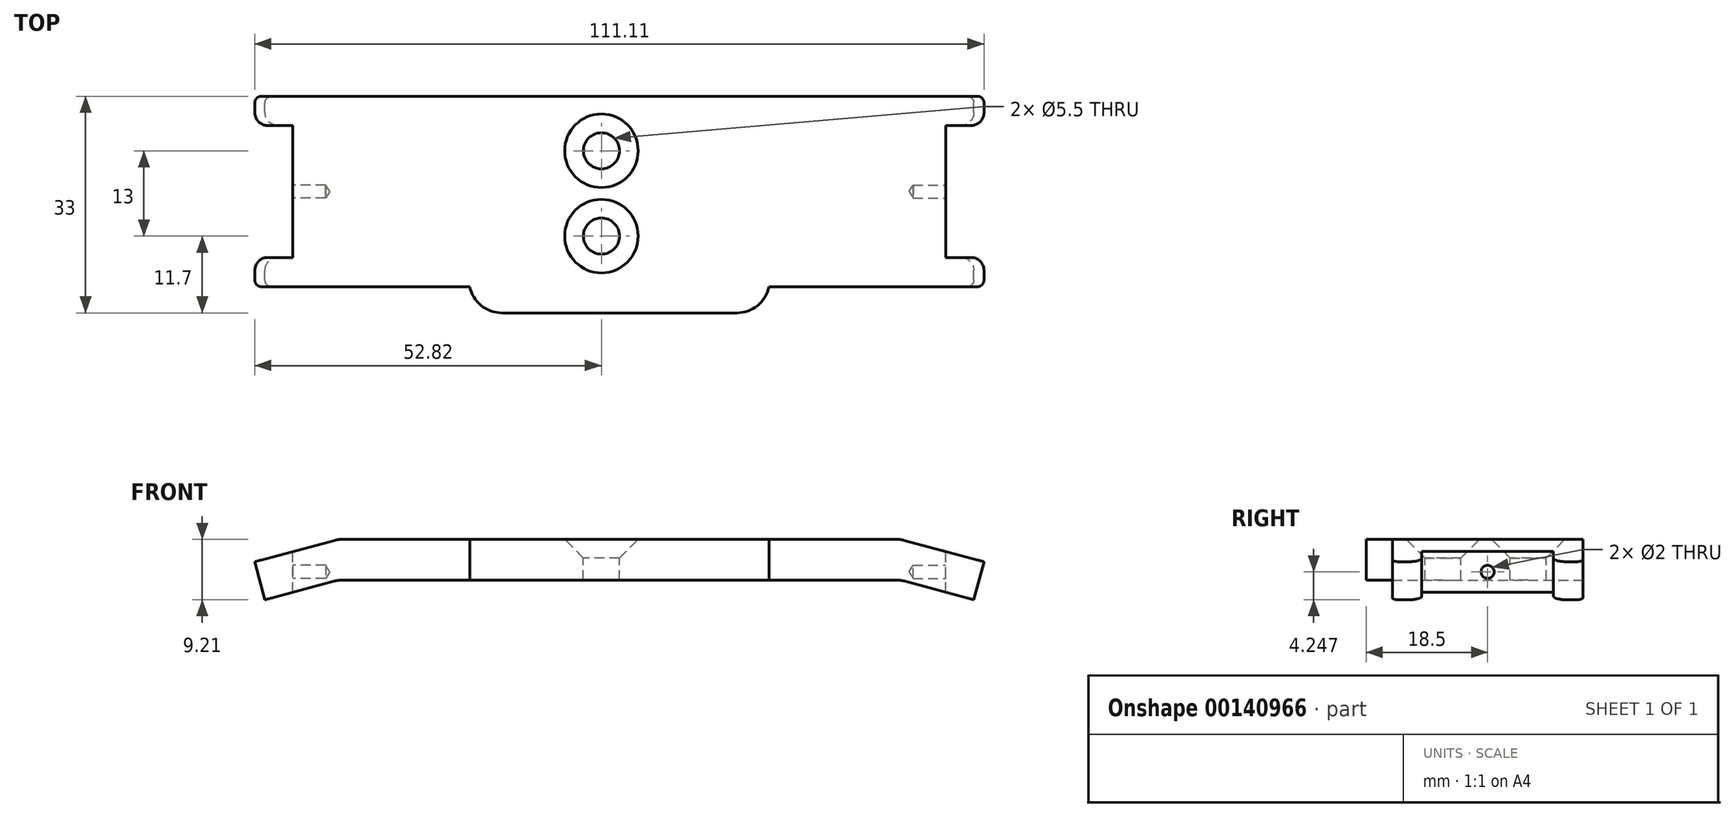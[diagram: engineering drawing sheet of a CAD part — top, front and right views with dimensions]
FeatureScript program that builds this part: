
annotation { "Feature Type Name" : "Feature", "Feature Type Description" : "" }
export const myFeature = defineFeature(function(context is Context, id is Id, definition is map)
    precondition{}
    {
        {
            var Q0;
            Q0=qCreatedBy(makeId("Front.planeOp"),FACE);
            var sketch = newSketch(context, id + "F0", { "sketchPlane" : qUnion([Q0])});
            skLineSegment(sketch, "E0", {"start": v(-40.07, 20.76) * mm, "end": v(45.54, 20.76) * mm});
            skLineSegment(sketch, "E1", {"start": v(45.54, 20.76) * mm, "end": v(58.3, 17.34) * mm});
            skLineSegment(sketch, "E2", {"start": v(58.3, 17.34) * mm, "end": v(56.74, 11.55) * mm});
            skLineSegment(sketch, "E3", {"start": v(56.74, 11.55) * mm, "end": v(45.54, 14.55) * mm});
            skLineSegment(sketch, "E4", {"start": v(45.54, 14.55) * mm, "end": v(-40.07, 14.55) * mm});
            skLineSegment(sketch, "E5", {"start": v(-40.07, 14.55) * mm, "end": v(-51.26, 11.55) * mm});
            skLineSegment(sketch, "E6", {"start": v(-51.26, 11.55) * mm, "end": v(-52.82, 17.34) * mm});
            skLineSegment(sketch, "E7", {"start": v(-52.82, 17.34) * mm, "end": v(-40.07, 20.76) * mm});
            skSolve(sketch);
        }
        {
            var Q0;
            Q0=makeQuery(id+"F0.imprint","IMPRINT",FACE,{"disambiguationData":[TD([[makeQuery(id+"F0.imprint","IMPRINT",EDGE,{"derivedFrom":sQuery(id+"F0.wireOp",EDGE,"E0")}),-1.0]])]});
            extrude(context, id + "F1", {"entities" : qUnion([Q0]), "depth" : 29 * mm});
        }
        {
            var Q0;
            Q0=makeQuery(id+"F1.opExtrude","CAP_FACE",FACE,{"disambiguationData":[OSD([sQuery(id+"F0.wireOp",EDGE,"E0"),sQuery(id+"F0.wireOp",EDGE,"E1"),sQuery(id+"F0.wireOp",EDGE,"E2"),sQuery(id+"F0.wireOp",EDGE,"E3"),sQuery(id+"F0.wireOp",EDGE,"E4"),sQuery(id+"F0.wireOp",EDGE,"E5"),sQuery(id+"F0.wireOp",EDGE,"E6"),sQuery(id+"F0.wireOp",EDGE,"E7")])],"isStart":false});
            var sketch = newSketch(context, id + "F2", { "sketchPlane" : qUnion([Q0])});
            skLineSegment(sketch, "E8.bottom", {"start": v(-20.07, 20.76) * mm, "end": v(25.54, 20.76) * mm});
            skLineSegment(sketch, "E8.top", {"start": v(-20.07, 14.55) * mm, "end": v(25.54, 14.55) * mm});
            skLineSegment(sketch, "E8.left", {"start": v(-20.07, 20.76) * mm, "end": v(-20.07, 14.55) * mm});
            skLineSegment(sketch, "E8.right", {"start": v(25.54, 20.76) * mm, "end": v(25.54, 14.55) * mm});
            skSolve(sketch);
        }
        {
            var Q0;
            Q0=makeQuery(id+"F2.imprint","IMPRINT",FACE,{"disambiguationData":[TD([[makeQuery(id+"F2.imprint","IMPRINT",EDGE,{"derivedFrom":sQuery(id+"F2.wireOp",EDGE,"E8.bottom")}),-1.0]])]});
            extrude(context, id + "F3", {"entities" : qUnion([Q0]), "operationType" : NewBodyOperationType.ADD, "depth" : 4 * mm, "offsetDistance" : 25 * mm});
        }
        {
            var Q0;
            Q0=makeQuery(id+"F3.boolean.opBoolean","MERGE",FACE,{"derivedFrom":[makeQuery(id+"F1.opExtrude","SWEPT_FACE",FACE,{"disambiguationData":[OSD([sQuery(id+"F0.wireOp",EDGE,"E0")])]}),makeQuery(id+"F3.opExtrude","SWEPT_FACE",FACE,{"disambiguationData":[OSD([sQuery(id+"F2.wireOp",EDGE,"E8.bottom")])]})]});
            var sketch = newSketch(context, id + "F4", { "sketchPlane" : qUnion([Q0])});
            skLineSegment(sketch, "E9.bottom", {"start": v(-61.47, -4.45) * mm, "end": v(-47.02, -4.45) * mm});
            skLineSegment(sketch, "E9.top", {"start": v(-61.47, -24.55) * mm, "end": v(-47.02, -24.55) * mm});
            skLineSegment(sketch, "E9.left", {"start": v(-61.47, -4.45) * mm, "end": v(-61.47, -24.55) * mm});
            skLineSegment(sketch, "E9.right", {"start": v(-47.02, -4.45) * mm, "end": v(-47.02, -24.55) * mm});
            skLineSegment(sketch, "E10.bottom", {"start": v(52.5, -4.45) * mm, "end": v(64.3, -4.45) * mm});
            skLineSegment(sketch, "E10.top", {"start": v(52.5, -24.55) * mm, "end": v(64.3, -24.55) * mm});
            skLineSegment(sketch, "E10.left", {"start": v(64.3, -4.45) * mm, "end": v(64.3, -24.55) * mm});
            skLineSegment(sketch, "E10.right", {"start": v(52.5, -4.45) * mm, "end": v(52.5, -24.55) * mm});
            skSolve(sketch);
        }
        {
            var Q0;
            Q0=makeQuery(id+"F4.imprint","IMPRINT",FACE,{"disambiguationData":[TD([[makeQuery(id+"F4.imprint","IMPRINT",EDGE,{"derivedFrom":sQuery(id+"F4.wireOp",EDGE,"E9.bottom")}),-1.0]])]});
            var Q1;
            Q1=makeQuery(id+"F4.imprint","IMPRINT",FACE,{"disambiguationData":[TD([[makeQuery(id+"F4.imprint","IMPRINT",EDGE,{"derivedFrom":sQuery(id+"F4.wireOp",EDGE,"E10.bottom")}),-1.0]])]});
            extrude(context, id + "F5", {"entities" : qUnion([Q0, Q1]), "operationType" : NewBodyOperationType.REMOVE, "oppositeDirection" : true, "depth" : 25 * mm});
        }
        {
            var Q0;
            Q0=makeQuery(id+"F5.boolean.opBoolean","COPY",FACE,{"derivedFrom":makeQuery(id+"F5.opExtrude","SWEPT_FACE",FACE,{"disambiguationData":[OSD([sQuery(id+"F4.wireOp",EDGE,"E9.right")])]})});
            var sketch = newSketch(context, id + "F6", { "sketchPlane" : qUnion([Q0])});
            skCircle(sketch, "E11", {"center": v(14.5, 15.8) * mm, "radius": 1.07 * mm});
            skSolve(sketch);
        }
        {
            var Q0;
            Q0=sQuery(id+"F6.wireOp",VERTEX,"E11.center");
            var Q1;
            Q1=makeQuery(id+"F1.opExtrude","SWEPT_BODY",BODY,{"disambiguationData":[OSD([sQuery(id+"F0.wireOp",EDGE,"E0"),sQuery(id+"F0.wireOp",EDGE,"E1"),sQuery(id+"F0.wireOp",EDGE,"E2"),sQuery(id+"F0.wireOp",EDGE,"E3"),sQuery(id+"F0.wireOp",EDGE,"E4"),sQuery(id+"F0.wireOp",EDGE,"E5"),sQuery(id+"F0.wireOp",EDGE,"E6"),sQuery(id+"F0.wireOp",EDGE,"E7")])]});
            hole(context, id + "F7", {"style" : HoleStyle.SIMPLE, "endStyle" : HoleEndStyle.BLIND, "holeDiameter" : 2 * mm, "holeDepth" : 5 * mm, "isTappedThrough" : true, "tappedDepth" : 12 * mm, "tapClearance" : 3, "locations" : qUnion([Q0]), "scope" : qUnion([Q1])});
        }
        {
            var Q0;
            Q0=makeQuery(id+"F1.opExtrude","SWEPT_EDGE",EDGE,{"disambiguationData":[OSD([sQuery(id+"F0.wireOp",EDGE,"E0"),sQuery(id+"F0.wireOp",EDGE,"E1")])]});
            var Q1;
            Q1=makeQuery(id+"F1.opExtrude","SWEPT_EDGE",EDGE,{"disambiguationData":[OSD([sQuery(id+"F0.wireOp",EDGE,"E0"),sQuery(id+"F0.wireOp",EDGE,"E7")])]});
            var Q2;
            Q2=makeQuery(id+"F3.opExtrude","CAP_EDGE",EDGE,{"disambiguationData":[OSD([sQuery(id+"F2.wireOp",EDGE,"E8.left")])],"isStart":false});
            var Q3;
            Q3=makeQuery(id+"F3.opExtrude","CAP_EDGE",EDGE,{"disambiguationData":[OSD([sQuery(id+"F2.wireOp",EDGE,"E8.right")])],"isStart":false});
            var Q4;
            Q4=makeQuery(id+"F1.opExtrude","SWEPT_EDGE",EDGE,{"disambiguationData":[OSD([sQuery(id+"F0.wireOp",EDGE,"E4"),sQuery(id+"F0.wireOp",EDGE,"E5")])]});
            var Q5;
            Q5=makeQuery(id+"F1.opExtrude","SWEPT_EDGE",EDGE,{"disambiguationData":[OSD([sQuery(id+"F0.wireOp",EDGE,"E3"),sQuery(id+"F0.wireOp",EDGE,"E4")])]});
            fillet(context, id + "F8", {"entities" : qUnion([Q0, Q1, Q2, Q3, Q4, Q5]), "radius" : 5 * mm, "tangentPropagation" : true, "allowEdgeOverflow" : false});
        }
        {
            var Q0;
            Q0=makeQuery(id+"F1.opExtrude","CAP_EDGE",EDGE,{"disambiguationData":[OSD([sQuery(id+"F0.wireOp",EDGE,"E6")])],"isStart":false});
            var Q1;
            Q1=makeQuery(id+"F1.opExtrude","CAP_EDGE",EDGE,{"disambiguationData":[OSD([sQuery(id+"F0.wireOp",EDGE,"E6")])],"isStart":true});
            var Q2;
            Q2=makeQuery(id+"F1.opExtrude","CAP_EDGE",EDGE,{"disambiguationData":[OSD([sQuery(id+"F0.wireOp",EDGE,"E2")])],"isStart":true});
            var Q3;
            Q3=makeQuery(id+"F1.opExtrude","CAP_EDGE",EDGE,{"disambiguationData":[OSD([sQuery(id+"F0.wireOp",EDGE,"E2")])],"isStart":false});
            fillet(context, id + "F9", {"entities" : qUnion([Q0, Q1, Q2, Q3]), "radius" : 1 * mm, "tangentPropagation" : true, "allowEdgeOverflow" : false});
        }
        {
            var Q0;
            Q0=makeQuery(id+"F5.boolean.opBoolean","COPY",FACE,{"derivedFrom":makeQuery(id+"F5.opExtrude","SWEPT_FACE",FACE,{"disambiguationData":[OSD([sQuery(id+"F4.wireOp",EDGE,"E10.right")])]})});
            var sketch = newSketch(context, id + "F10", { "sketchPlane" : qUnion([Q0])});
            skCircle(sketch, "E12", {"center": v(-14.5, 15.8) * mm, "radius": 1.68 * mm});
            skSolve(sketch);
        }
        {
            var Q0;
            Q0=sQuery(id+"F10.wireOp",VERTEX,"E12.center");
            var Q1;
            Q1=makeQuery(id+"F1.opExtrude","SWEPT_BODY",BODY,{"disambiguationData":[OSD([sQuery(id+"F0.wireOp",EDGE,"E0"),sQuery(id+"F0.wireOp",EDGE,"E1"),sQuery(id+"F0.wireOp",EDGE,"E2"),sQuery(id+"F0.wireOp",EDGE,"E3"),sQuery(id+"F0.wireOp",EDGE,"E4"),sQuery(id+"F0.wireOp",EDGE,"E5"),sQuery(id+"F0.wireOp",EDGE,"E6"),sQuery(id+"F0.wireOp",EDGE,"E7")])]});
            hole(context, id + "F11", {"style" : HoleStyle.SIMPLE, "endStyle" : HoleEndStyle.BLIND, "holeDiameter" : 2 * mm, "holeDepth" : 5 * mm, "isTappedThrough" : true, "tappedDepth" : 12 * mm, "tapClearance" : 3, "locations" : qUnion([Q0]), "scope" : qUnion([Q1])});
        }
        {
            var Q0;
            Q0=makeQuery(id+"F5.boolean.opBoolean","INTERSECT",EDGE,{"derivedFrom":[makeQuery(id+"F1.opExtrude","SWEPT_FACE",FACE,{"disambiguationData":[OSD([sQuery(id+"F0.wireOp",EDGE,"E6")])]}),makeQuery(id+"F5.opExtrude","SWEPT_FACE",FACE,{"disambiguationData":[OSD([sQuery(id+"F4.wireOp",EDGE,"E9.top")])]})]});
            var Q1;
            Q1=makeQuery(id+"F5.boolean.opBoolean","INTERSECT",EDGE,{"derivedFrom":[makeQuery(id+"F1.opExtrude","SWEPT_FACE",FACE,{"disambiguationData":[OSD([sQuery(id+"F0.wireOp",EDGE,"E6")])]}),makeQuery(id+"F5.opExtrude","SWEPT_FACE",FACE,{"disambiguationData":[OSD([sQuery(id+"F4.wireOp",EDGE,"E9.bottom")])]})]});
            var Q2;
            Q2=makeQuery(id+"F5.boolean.opBoolean","INTERSECT",EDGE,{"derivedFrom":[makeQuery(id+"F1.opExtrude","SWEPT_FACE",FACE,{"disambiguationData":[OSD([sQuery(id+"F0.wireOp",EDGE,"E2")])]}),makeQuery(id+"F5.opExtrude","SWEPT_FACE",FACE,{"disambiguationData":[OSD([sQuery(id+"F4.wireOp",EDGE,"E10.top")])]})]});
            var Q3;
            Q3=makeQuery(id+"F5.boolean.opBoolean","INTERSECT",EDGE,{"derivedFrom":[makeQuery(id+"F1.opExtrude","SWEPT_FACE",FACE,{"disambiguationData":[OSD([sQuery(id+"F0.wireOp",EDGE,"E2")])]}),makeQuery(id+"F5.opExtrude","SWEPT_FACE",FACE,{"disambiguationData":[OSD([sQuery(id+"F4.wireOp",EDGE,"E10.bottom")])]})]});
            fillet(context, id + "F12", {"entities" : qUnion([Q0, Q1, Q2, Q3]), "radius" : 2 * mm, "tangentPropagation" : true, "allowEdgeOverflow" : false});
        }
        {
            var Q0;
            Q0=makeQuery(id+"F3.boolean.opBoolean","MERGE",FACE,{"derivedFrom":[makeQuery(id+"F1.opExtrude","SWEPT_FACE",FACE,{"disambiguationData":[OSD([sQuery(id+"F0.wireOp",EDGE,"E0")])]}),makeQuery(id+"F3.opExtrude","SWEPT_FACE",FACE,{"disambiguationData":[OSD([sQuery(id+"F2.wireOp",EDGE,"E8.bottom")])]})]});
            var sketch = newSketch(context, id + "F13", { "sketchPlane" : qUnion([Q0])});
            skCircle(sketch, "E13", {"center": v(0, -8.3) * mm, "radius": 3 * mm});
            skCircle(sketch, "E14", {"center": v(0, -21.3) * mm, "radius": 2.9 * mm});
            skSolve(sketch);
        }
        {
            var Q0;
            Q0=sQuery(id+"F13.wireOp",VERTEX,"E14.center");
            var Q1;
            Q1=sQuery(id+"F13.wireOp",VERTEX,"E13.center");
            var Q2;
            Q2=makeQuery(id+"F1.opExtrude","SWEPT_BODY",BODY,{"disambiguationData":[OSD([sQuery(id+"F0.wireOp",EDGE,"E0"),sQuery(id+"F0.wireOp",EDGE,"E1"),sQuery(id+"F0.wireOp",EDGE,"E2"),sQuery(id+"F0.wireOp",EDGE,"E3"),sQuery(id+"F0.wireOp",EDGE,"E4"),sQuery(id+"F0.wireOp",EDGE,"E5"),sQuery(id+"F0.wireOp",EDGE,"E6"),sQuery(id+"F0.wireOp",EDGE,"E7")])]});
            hole(context, id + "F14", {"style" : HoleStyle.C_SINK, "endStyle" : HoleEndStyle.THROUGH, "standardTappedOrClearance" : lookupTablePath({ "standard" : "ISO", "fit" : "Normal", "size" : "M5", "type" : "Clearance" }), "standardBlindInLast" : lookupTablePath({ "fit" : "Standard", "standard" : "ISO", "size" : "M5", "type" : "Clearance" }), "holeDiameter" : 5.5 * mm, "cSinkDiameter" : 11.2 * mm, "cSinkAngle" : 90 * degree, "majorDiameter" : 5 * mm, "isTappedThrough" : true, "tappedDepth" : 12 * mm, "tapClearance" : 3, "locations" : qUnion([Q0, Q1]), "scope" : qUnion([Q2])});
        }
    });
